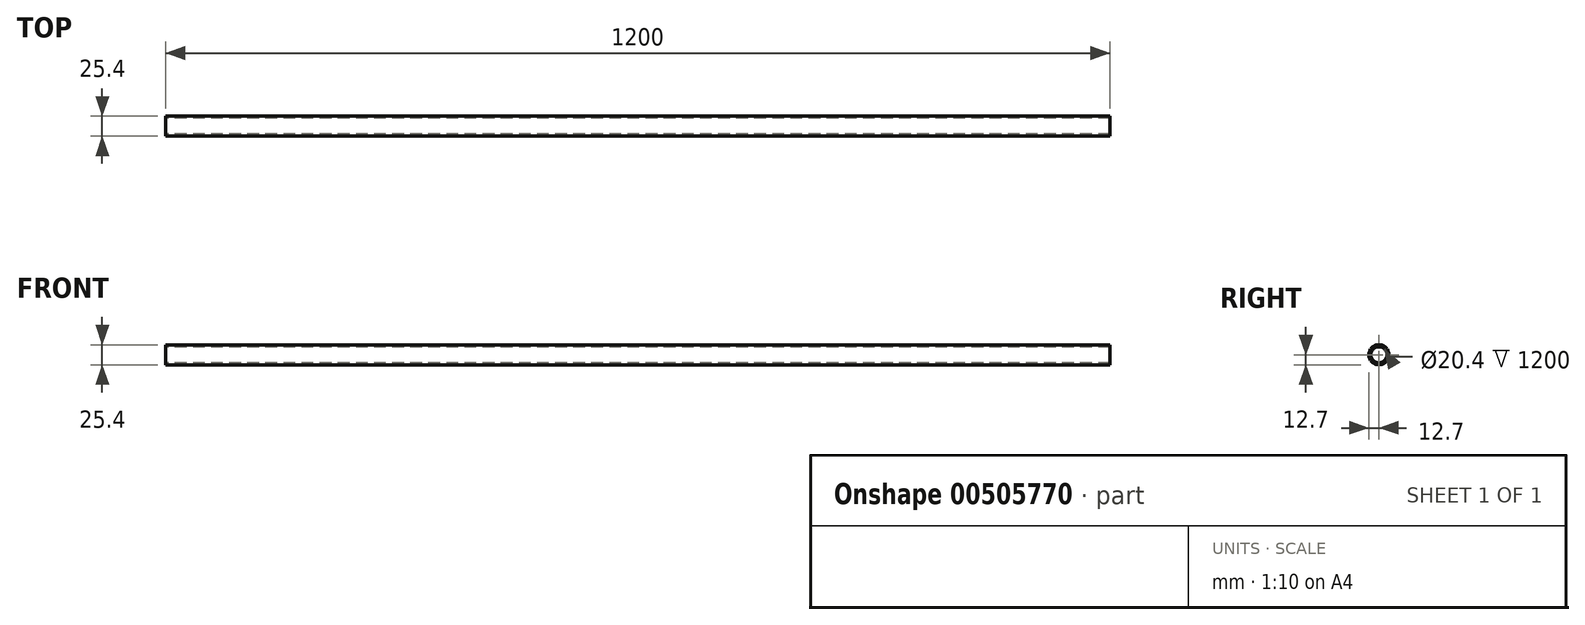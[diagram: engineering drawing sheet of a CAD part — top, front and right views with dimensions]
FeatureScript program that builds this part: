
annotation { "Feature Type Name" : "Feature", "Feature Type Description" : "" }
export const myFeature = defineFeature(function(context is Context, id is Id, definition is map)
    precondition{}
    {
        {
            var Q0;
            Q0=qCreatedBy(makeId("Right.planeOp"),FACE);
            var sketch = newSketch(context, id + "F0", { "sketchPlane" : qUnion([Q0])});
            skCircle(sketch, "E0", {"center": v(0, 0) * mm, "radius": 12.7 * mm});
            skSolve(sketch);
        }
        {
            var Q0;
            Q0 = qSketchRegion(id + "F0", true);
            extrude(context, id + "F1", {"entities" : qUnion([Q0]), "endBound" : BoundingType.SYMMETRIC, "depth" : 1200 * mm});
        }
        {
            var Q0;
            Q0=makeQuery(id+"F1.opExtrude","CAP_FACE",FACE,{"disambiguationData":[OSD([sQuery(id+"F0.wireOp",EDGE,"E0")])],"isStart":false});
            var Q1;
            Q1=makeQuery(id+"F1.opExtrude","CAP_FACE",FACE,{"disambiguationData":[OSD([sQuery(id+"F0.wireOp",EDGE,"E0")])],"isStart":true});
            shell(context, id + "F2", {"entities" : qUnion([Q0, Q1]), "thickness" : 2.5 * mm});
        }
    });
